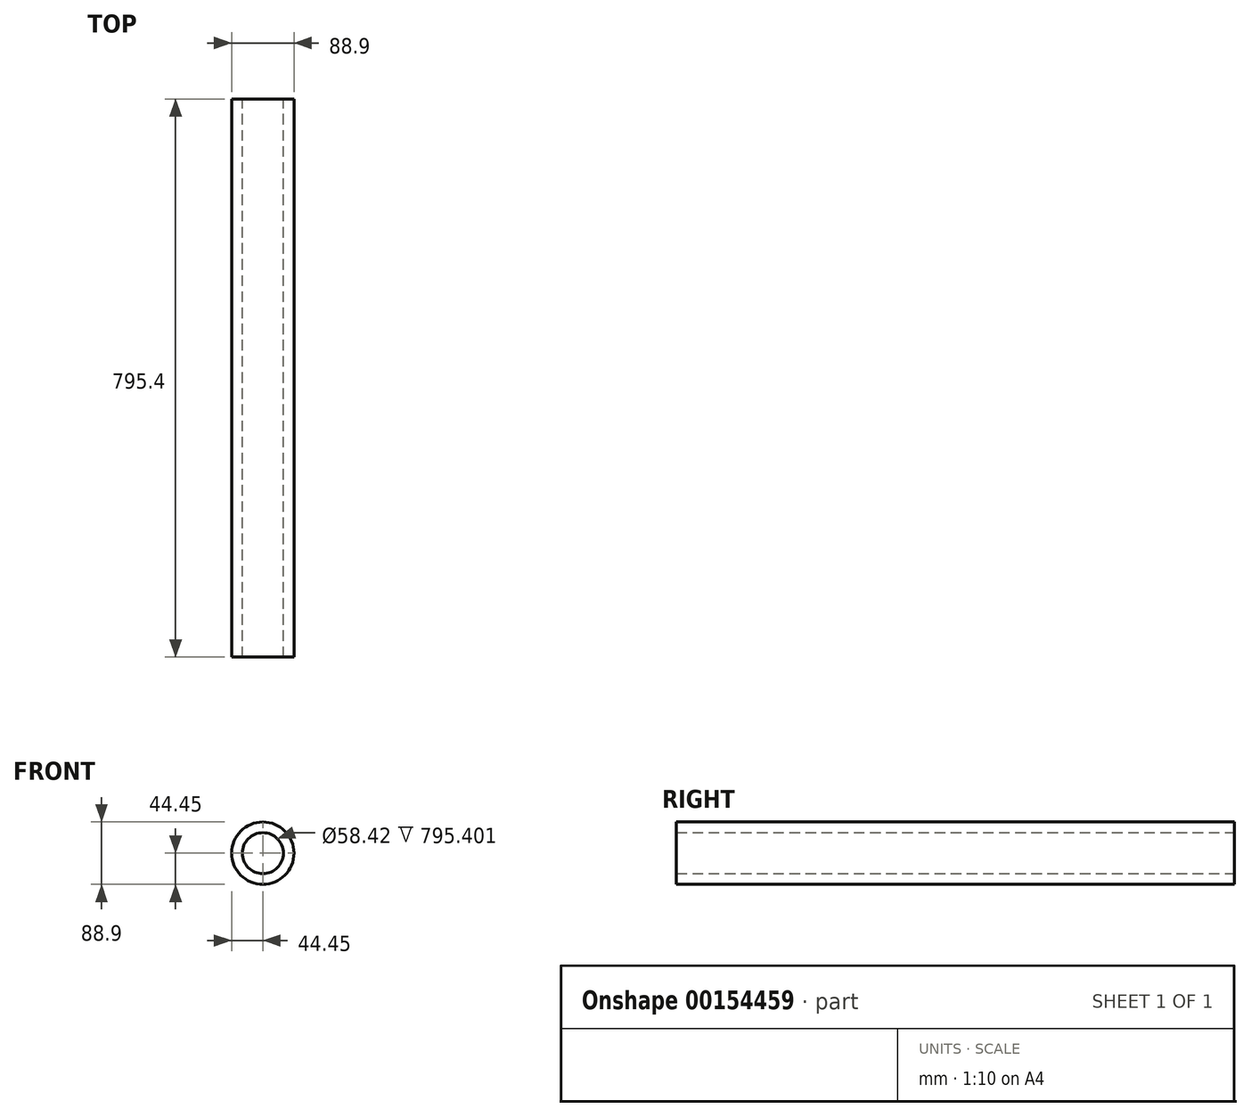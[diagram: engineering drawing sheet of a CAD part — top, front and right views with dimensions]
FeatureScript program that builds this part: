
annotation { "Feature Type Name" : "Feature", "Feature Type Description" : "" }
export const myFeature = defineFeature(function(context is Context, id is Id, definition is map)
    precondition{}
    {
        {
            var Q0;
            Q0=qCreatedBy(makeId("Front.planeOp"),FACE);
            var sketch = newSketch(context, id + "F0", { "sketchPlane" : qUnion([Q0])});
            skCircle(sketch, "E0", {"center": v(0, 0) * mm, "radius": 44.45 * mm});
            skCircle(sketch, "E1.0", {"center": v(0, 0) * mm, "radius": 29.21 * mm});
            skSolve(sketch);
        }
        {
            var Q0;
            Q0=makeQuery(id+"F0.imprint","IMPRINT",FACE,{"disambiguationData":[TD([[makeQuery(id+"F0.imprint","IMPRINT",EDGE,{"derivedFrom":sQuery(id+"F0.wireOp",EDGE,"E0")}),1.0]])]});
            extrude(context, id + "F1", {"entities" : qUnion([Q0]), "depth" : 795.4 * mm});
        }
    });
